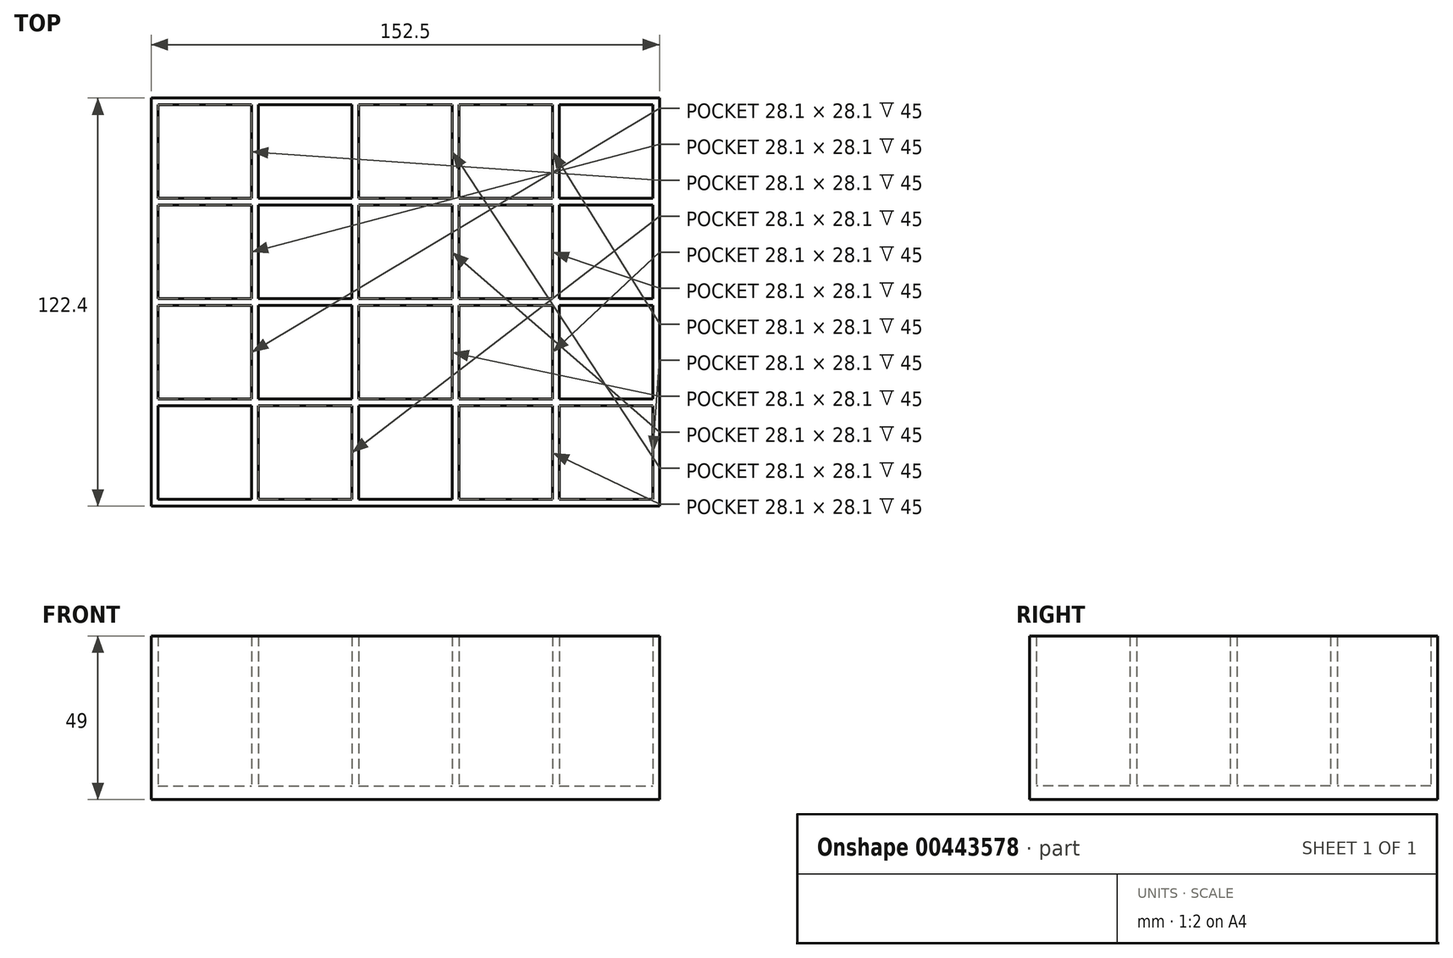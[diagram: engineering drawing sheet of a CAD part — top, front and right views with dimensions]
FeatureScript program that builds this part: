
annotation { "Feature Type Name" : "Feature", "Feature Type Description" : "" }
export const myFeature = defineFeature(function(context is Context, id is Id, definition is map)
    precondition{}
    {
        {
            var Q0;
            Q0=qCreatedBy(makeId("Top.planeOp"),FACE);
            var sketch = newSketch(context, id + "F0", { "sketchPlane" : qUnion([Q0])});
            skLineSegment(sketch, "E0.bottom", {"start": v(0, 0) * mm, "end": v(28.1, 0) * mm});
            skLineSegment(sketch, "E0.top", {"start": v(0, -28.1) * mm, "end": v(28.1, -28.1) * mm});
            skLineSegment(sketch, "E0.left", {"start": v(0, 0) * mm, "end": v(0, -28.1) * mm});
            skLineSegment(sketch, "E0.right", {"start": v(28.1, 0) * mm, "end": v(28.1, -28.1) * mm});
            skLineSegment(sketch, "E1.0.1.0", {"start": v(0, 30.1) * mm, "end": v(28.1, 30.1) * mm});
            skLineSegment(sketch, "E1.0.1.1", {"start": v(0, 30.1) * mm, "end": v(0, 2) * mm});
            skLineSegment(sketch, "E1.0.1.2", {"start": v(0, 2) * mm, "end": v(28.1, 2) * mm});
            skLineSegment(sketch, "E1.0.1.3", {"start": v(28.1, 30.1) * mm, "end": v(28.1, 2) * mm});
            skLineSegment(sketch, "E1.0.2.0", {"start": v(0, 60.2) * mm, "end": v(28.1, 60.2) * mm});
            skLineSegment(sketch, "E1.0.2.1", {"start": v(0, 60.2) * mm, "end": v(0, 32.1) * mm});
            skLineSegment(sketch, "E1.0.2.2", {"start": v(0, 32.1) * mm, "end": v(28.1, 32.1) * mm});
            skLineSegment(sketch, "E1.0.2.3", {"start": v(28.1, 60.2) * mm, "end": v(28.1, 32.1) * mm});
            skLineSegment(sketch, "E1.0.3.0", {"start": v(0, 90.3) * mm, "end": v(28.1, 90.3) * mm});
            skLineSegment(sketch, "E1.0.3.1", {"start": v(0, 90.3) * mm, "end": v(0, 62.2) * mm});
            skLineSegment(sketch, "E1.0.3.2", {"start": v(0, 62.2) * mm, "end": v(28.1, 62.2) * mm});
            skLineSegment(sketch, "E1.0.3.3", {"start": v(28.1, 90.3) * mm, "end": v(28.1, 62.2) * mm});
            skLineSegment(sketch, "E1.1.0.0", {"start": v(30.1, 0) * mm, "end": v(58.2, 0) * mm});
            skLineSegment(sketch, "E1.1.0.1", {"start": v(30.1, 0) * mm, "end": v(30.1, -28.1) * mm});
            skLineSegment(sketch, "E1.1.0.2", {"start": v(30.1, -28.1) * mm, "end": v(58.2, -28.1) * mm});
            skLineSegment(sketch, "E1.1.0.3", {"start": v(58.2, 0) * mm, "end": v(58.2, -28.1) * mm});
            skLineSegment(sketch, "E1.1.1.0", {"start": v(30.1, 30.1) * mm, "end": v(58.2, 30.1) * mm});
            skLineSegment(sketch, "E1.1.1.1", {"start": v(30.1, 30.1) * mm, "end": v(30.1, 2) * mm});
            skLineSegment(sketch, "E1.1.1.2", {"start": v(30.1, 2) * mm, "end": v(58.2, 2) * mm});
            skLineSegment(sketch, "E1.1.1.3", {"start": v(58.2, 30.1) * mm, "end": v(58.2, 2) * mm});
            skLineSegment(sketch, "E1.1.2.0", {"start": v(30.1, 60.2) * mm, "end": v(58.2, 60.2) * mm});
            skLineSegment(sketch, "E1.1.2.1", {"start": v(30.1, 60.2) * mm, "end": v(30.1, 32.1) * mm});
            skLineSegment(sketch, "E1.1.2.2", {"start": v(30.1, 32.1) * mm, "end": v(58.2, 32.1) * mm});
            skLineSegment(sketch, "E1.1.2.3", {"start": v(58.2, 60.2) * mm, "end": v(58.2, 32.1) * mm});
            skLineSegment(sketch, "E1.1.3.0", {"start": v(30.1, 90.3) * mm, "end": v(58.2, 90.3) * mm});
            skLineSegment(sketch, "E1.1.3.1", {"start": v(30.1, 90.3) * mm, "end": v(30.1, 62.2) * mm});
            skLineSegment(sketch, "E1.1.3.2", {"start": v(30.1, 62.2) * mm, "end": v(58.2, 62.2) * mm});
            skLineSegment(sketch, "E1.1.3.3", {"start": v(58.2, 90.3) * mm, "end": v(58.2, 62.2) * mm});
            skLineSegment(sketch, "E1.2.0.0", {"start": v(60.2, 0) * mm, "end": v(88.3, 0) * mm});
            skLineSegment(sketch, "E1.2.0.1", {"start": v(60.2, 0) * mm, "end": v(60.2, -28.1) * mm});
            skLineSegment(sketch, "E1.2.0.2", {"start": v(60.2, -28.1) * mm, "end": v(88.3, -28.1) * mm});
            skLineSegment(sketch, "E1.2.0.3", {"start": v(88.3, 0) * mm, "end": v(88.3, -28.1) * mm});
            skLineSegment(sketch, "E1.2.1.0", {"start": v(60.2, 30.1) * mm, "end": v(88.3, 30.1) * mm});
            skLineSegment(sketch, "E1.2.1.1", {"start": v(60.2, 30.1) * mm, "end": v(60.2, 2) * mm});
            skLineSegment(sketch, "E1.2.1.2", {"start": v(60.2, 2) * mm, "end": v(88.3, 2) * mm});
            skLineSegment(sketch, "E1.2.1.3", {"start": v(88.3, 30.1) * mm, "end": v(88.3, 2) * mm});
            skLineSegment(sketch, "E1.2.2.0", {"start": v(60.2, 60.2) * mm, "end": v(88.3, 60.2) * mm});
            skLineSegment(sketch, "E1.2.2.1", {"start": v(60.2, 60.2) * mm, "end": v(60.2, 32.1) * mm});
            skLineSegment(sketch, "E1.2.2.2", {"start": v(60.2, 32.1) * mm, "end": v(88.3, 32.1) * mm});
            skLineSegment(sketch, "E1.2.2.3", {"start": v(88.3, 60.2) * mm, "end": v(88.3, 32.1) * mm});
            skLineSegment(sketch, "E1.2.3.0", {"start": v(60.2, 90.3) * mm, "end": v(88.3, 90.3) * mm});
            skLineSegment(sketch, "E1.2.3.1", {"start": v(60.2, 90.3) * mm, "end": v(60.2, 62.2) * mm});
            skLineSegment(sketch, "E1.2.3.2", {"start": v(60.2, 62.2) * mm, "end": v(88.3, 62.2) * mm});
            skLineSegment(sketch, "E1.2.3.3", {"start": v(88.3, 90.3) * mm, "end": v(88.3, 62.2) * mm});
            skLineSegment(sketch, "E1.3.0.0", {"start": v(90.3, 0) * mm, "end": v(118.4, 0) * mm});
            skLineSegment(sketch, "E1.3.0.1", {"start": v(90.3, 0) * mm, "end": v(90.3, -28.1) * mm});
            skLineSegment(sketch, "E1.3.0.2", {"start": v(90.3, -28.1) * mm, "end": v(118.4, -28.1) * mm});
            skLineSegment(sketch, "E1.3.0.3", {"start": v(118.4, 0) * mm, "end": v(118.4, -28.1) * mm});
            skLineSegment(sketch, "E1.3.1.0", {"start": v(90.3, 30.1) * mm, "end": v(118.4, 30.1) * mm});
            skLineSegment(sketch, "E1.3.1.1", {"start": v(90.3, 30.1) * mm, "end": v(90.3, 2) * mm});
            skLineSegment(sketch, "E1.3.1.2", {"start": v(90.3, 2) * mm, "end": v(118.4, 2) * mm});
            skLineSegment(sketch, "E1.3.1.3", {"start": v(118.4, 30.1) * mm, "end": v(118.4, 2) * mm});
            skLineSegment(sketch, "E1.3.2.0", {"start": v(90.3, 60.2) * mm, "end": v(118.4, 60.2) * mm});
            skLineSegment(sketch, "E1.3.2.1", {"start": v(90.3, 60.2) * mm, "end": v(90.3, 32.1) * mm});
            skLineSegment(sketch, "E1.3.2.2", {"start": v(90.3, 32.1) * mm, "end": v(118.4, 32.1) * mm});
            skLineSegment(sketch, "E1.3.2.3", {"start": v(118.4, 60.2) * mm, "end": v(118.4, 32.1) * mm});
            skLineSegment(sketch, "E1.3.3.0", {"start": v(90.3, 90.3) * mm, "end": v(118.4, 90.3) * mm});
            skLineSegment(sketch, "E1.3.3.1", {"start": v(90.3, 90.3) * mm, "end": v(90.3, 62.2) * mm});
            skLineSegment(sketch, "E1.3.3.2", {"start": v(90.3, 62.2) * mm, "end": v(118.4, 62.2) * mm});
            skLineSegment(sketch, "E1.3.3.3", {"start": v(118.4, 90.3) * mm, "end": v(118.4, 62.2) * mm});
            skLineSegment(sketch, "E1.4.0.0", {"start": v(120.4, 0) * mm, "end": v(148.5, 0) * mm});
            skLineSegment(sketch, "E1.4.0.1", {"start": v(120.4, 0) * mm, "end": v(120.4, -28.1) * mm});
            skLineSegment(sketch, "E1.4.0.2", {"start": v(120.4, -28.1) * mm, "end": v(148.5, -28.1) * mm});
            skLineSegment(sketch, "E1.4.0.3", {"start": v(148.5, 0) * mm, "end": v(148.5, -28.1) * mm});
            skLineSegment(sketch, "E1.4.1.0", {"start": v(120.4, 30.1) * mm, "end": v(148.5, 30.1) * mm});
            skLineSegment(sketch, "E1.4.1.1", {"start": v(120.4, 30.1) * mm, "end": v(120.4, 2) * mm});
            skLineSegment(sketch, "E1.4.1.2", {"start": v(120.4, 2) * mm, "end": v(148.5, 2) * mm});
            skLineSegment(sketch, "E1.4.1.3", {"start": v(148.5, 30.1) * mm, "end": v(148.5, 2) * mm});
            skLineSegment(sketch, "E1.4.2.0", {"start": v(120.4, 60.2) * mm, "end": v(148.5, 60.2) * mm});
            skLineSegment(sketch, "E1.4.2.1", {"start": v(120.4, 60.2) * mm, "end": v(120.4, 32.1) * mm});
            skLineSegment(sketch, "E1.4.2.2", {"start": v(120.4, 32.1) * mm, "end": v(148.5, 32.1) * mm});
            skLineSegment(sketch, "E1.4.2.3", {"start": v(148.5, 60.2) * mm, "end": v(148.5, 32.1) * mm});
            skLineSegment(sketch, "E1.4.3.0", {"start": v(120.4, 90.3) * mm, "end": v(148.5, 90.3) * mm});
            skLineSegment(sketch, "E1.4.3.1", {"start": v(120.4, 90.3) * mm, "end": v(120.4, 62.2) * mm});
            skLineSegment(sketch, "E1.4.3.2", {"start": v(120.4, 62.2) * mm, "end": v(148.5, 62.2) * mm});
            skLineSegment(sketch, "E1.4.3.3", {"start": v(148.5, 90.3) * mm, "end": v(148.5, 62.2) * mm});
            skLineSegment(sketch, "E1.direction1", {"start": v(0, 0) * mm, "end": v(30.1, 0) * mm, "construction": true});
            skLineSegment(sketch, "E1.direction2", {"start": v(0, 0) * mm, "end": v(0, 30.1) * mm, "construction": true});
            skSolve(sketch);
        }
        {
            var Q0;
            Q0=qCreatedBy(makeId("Top.planeOp"),FACE);
            var sketch = newSketch(context, id + "F1", { "sketchPlane" : qUnion([Q0])});
            skLineSegment(sketch, "E2.bottom", {"start": v(-2, -30.1) * mm, "end": v(150.5, -30.1) * mm});
            skLineSegment(sketch, "E2.top", {"start": v(-2, 92.3) * mm, "end": v(150.5, 92.3) * mm});
            skLineSegment(sketch, "E2.left", {"start": v(-2, -30.1) * mm, "end": v(-2, 92.3) * mm});
            skLineSegment(sketch, "E2.right", {"start": v(150.5, -30.1) * mm, "end": v(150.5, 92.3) * mm});
            skPoint(sketch, "E3.0", {"position": v(0, -28.1) * mm});
            skPoint(sketch, "E4.0", {"position": v(0, 90.3) * mm});
            skPoint(sketch, "E5.0", {"position": v(148.5, -28.1) * mm});
            skSolve(sketch);
        }
        {
            var Q0;
            Q0 = qSketchRegion(id + "F1", true);
            extrude(context, id + "F2", {"entities" : qUnion([Q0]), "oppositeDirection" : true, "depth" : 4 * mm});
        }
        {
            var Q0;
            Q0 = qSketchRegion(id + "F1", true);
            extrude(context, id + "F3", {"entities" : qUnion([Q0]), "operationType" : NewBodyOperationType.ADD, "depth" : 45 * mm});
        }
        {
            var Q0;
            Q0 = qSketchRegion(id + "F0", true);
            extrude(context, id + "F4", {"entities" : qUnion([Q0]), "operationType" : NewBodyOperationType.REMOVE, "endBound" : BoundingType.THROUGH_ALL, "depth" : 25 * mm});
        }
    });
